# Revit family: RN 56000 Therm-Control-Set di regolazione DN 25 completo
name_source: partatom
category: HLS-Bauteile
units: mm (PartAtom-declared; Revit-internal decimal feet)

## family parameters
Arbeitsebenenbasiert = Nein
Beim Laden mit Abzugskörper schneiden = Nein
Bemaßung runder Anschluss = Durchmesser verwenden
Gemeinsam genutzt = Nein
Immer vertikal = Ja
Klassifizierung = Keine
Raumberechnungspunkt = Nein
Teiletyp = Ventil - Zerlegung in

## types (11) — shared parameters
1.010.00.2 Blattnummer der Richtlinie = 2
1.010.00.3 Ausgabedatum (Monat) der Richtlinie = 201601
1.010.00.4 Herstellername = R. Nussbaum AG
1.010.00.5 Revisionsdatum der Datei = 20190514
1.010.00.6 Webadresse des Herstellers = http://www.nussbaum.ch
1.100.00.3 Sortiernummer für Anzeigereihenfolge = 3
1.100.00.4 Produktbezeichnung = Armaturen für Flächenheizungen
1.960/3L.00.8 Link (URL) = https://www.nussbaum.ch
2.700.00.4 Armaturentyp = 13
2.700.00.5 Nennweite DN = 25
2.700.00.7 Maximale Betriebstemperatur TB [°C] = 60
2.700.00.8 Maximaler Betriebsdruck (Arbeitsdruck) ps [1.0 · 102 Pa] = 6
CONNECTOR0_ref_dY = 27 mm
CONNECTOR1_DIAMETER_dZ_0r = 20 mm
CONNECTOR1_ref_dY = 27 mm
CONNECTOR2_DIAMETER_dX_0r = 25 mm  [stored 0.082021 ft]
CONNECTOR2_dX_00 = 105 mm
CONNECTOR2_dX_01 = 97 mm
CONNECTOR3_DIAMETER_dZ_0r = 20 mm
CONNECTOR4_DIAMETER_dZ_0r = 20 mm
Connector Visibility = Nein
EnclosingSpace Visibility = Nein

## per-type parameters (varying)
- DN 25: 1.800.00.3 TGA-Nummer=0030010000000000000000000000090070000000000000000100000000; 1.810.00.3 Hersteller-Bestellnummer=56000.21; 1.810.00.4 DATANORM-Nummer=56000.21; 1.810.00.6 GTIN-Nummer=7612945814289; 2.700.00.26 Produktbeschreibung=56000.21, Therm-Control-Regelset DN 25 komplett, Grundausstattung, DN=25; CONNECTOR0_DIAMETER_dZ_0r=20 mm; CONNECTOR0_dZ_00=21 mm; CONNECTOR0_dZ_01=28 mm  [stored 0.0918635 ft]; CONNECTOR0_ref_dX=13 mm  [stored 0.0426509 ft]; CONNECTOR0_ref_dZ=28 mm  [stored 0.0918635 ft]; CONNECTOR1_dZ_00=21 mm; CONNECTOR1_dZ_01=28 mm  [stored 0.0918635 ft]; CONNECTOR1_ref_dX=63 mm; CONNECTOR1_ref_dZ=28 mm  [stored 0.0918635 ft]; CONNECTOR2_ref_dX=97 mm; CONNECTOR2_ref_dY=44 mm; CONNECTOR2_ref_dZ=77 mm; CONNECTOR3_dZ_00=119 mm; CONNECTOR3_dZ_01=112 mm; CONNECTOR3_ref_dX=13 mm  [stored 0.0426509 ft]; CONNECTOR3_ref_dY=44 mm; CONNECTOR3_ref_dZ=112 mm; CONNECTOR4_dZ_00=119 mm; CONNECTOR4_dZ_01=112 mm; CONNECTOR4_ref_dX=63 mm; CONNECTOR4_ref_dY=44 mm; CONNECTOR4_ref_dZ=112 mm; CONNECTOR5_DIAMETER_dX_0r=25 mm  [stored 0.082021 ft]; CONNECTOR5_dX_00=105 mm; CONNECTOR5_dX_01=97 mm; CONNECTOR5_ref_dX=97 mm; CONNECTOR5_ref_dY=27 mm; CONNECTOR5_ref_dZ=123 mm; R. Nussbaum AG 56000.21 de Visibility=Ja; R. Nussbaum AG 56000.22 de Visibility=Nein; R. Nussbaum AG 56000.23 de Visibility=Nein; R. Nussbaum AG 56000.24 de Visibility=Nein; R. Nussbaum AG 56000.25 de Visibility=Nein; R. Nussbaum AG 56000.26 de Visibility=Nein; R. Nussbaum AG 56000.27 de Visibility=Nein; R. Nussbaum AG 56000.28 de Visibility=Nein; R. Nussbaum AG 56000.29 de Visibility=Nein; R. Nussbaum AG 56000.30 de Visibility=Nein; R. Nussbaum AG 56000.31 de Visibility=Nein
- DN 25 8: 1.800.00.3 TGA-Nummer=0030010000000000000000000000090070000000000000000200000000; 1.810.00.3 Hersteller-Bestellnummer=56000.22; 1.810.00.4 DATANORM-Nummer=56000.22; 1.810.00.6 GTIN-Nummer=7612945814296; 2.700.00.26 Produktbeschreibung=56000.22, Therm-Control-Regelset DN 25 komplett, Grundausstattung, DN=25; CONNECTOR0_DIAMETER_dZ_0r=20 mm; CONNECTOR0_dZ_00=27 mm; CONNECTOR0_dZ_01=35 mm; CONNECTOR0_ref_dX=10 mm  [stored 0.0328084 ft]; CONNECTOR0_ref_dZ=35 mm; CONNECTOR1_dZ_00=27 mm; CONNECTOR1_dZ_01=35 mm; CONNECTOR1_ref_dX=60 mm; CONNECTOR1_ref_dZ=35 mm; CONNECTOR2_ref_dX=106 mm; CONNECTOR2_ref_dY=27 mm; CONNECTOR2_ref_dZ=35 mm; CONNECTOR3_dZ_00=119 mm; CONNECTOR3_dZ_01=112 mm; CONNECTOR3_ref_dX=100 mm; CONNECTOR3_ref_dY=27 mm; CONNECTOR3_ref_dZ=28 mm  [stored 0.0918635 ft]; CONNECTOR4_dZ_00=113 mm; CONNECTOR4_dZ_01=105 mm; CONNECTOR4_ref_dX=6 mm  [stored 0.019685 ft]; CONNECTOR4_ref_dY=27 mm; CONNECTOR4_ref_dZ=105 mm; CONNECTOR5_DIAMETER_dX_0r=25 mm  [stored 0.082021 ft]; CONNECTOR5_dX_00=105 mm; CONNECTOR5_dX_01=97 mm; CONNECTOR5_ref_dX=56 mm; CONNECTOR5_ref_dY=27 mm; CONNECTOR5_ref_dZ=105 mm; R. Nussbaum AG 56000.21 de Visibility=Nein; R. Nussbaum AG 56000.22 de Visibility=Ja; R. Nussbaum AG 56000.23 de Visibility=Nein; R. Nussbaum AG 56000.24 de Visibility=Nein; R. Nussbaum AG 56000.25 de Visibility=Nein; R. Nussbaum AG 56000.26 de Visibility=Nein; R. Nussbaum AG 56000.27 de Visibility=Nein; R. Nussbaum AG 56000.28 de Visibility=Nein; R. Nussbaum AG 56000.29 de Visibility=Nein; R. Nussbaum AG 56000.30 de Visibility=Nein; R. Nussbaum AG 56000.31 de Visibility=Nein
- DN 25 4: 1.800.00.3 TGA-Nummer=0030010000000000000000000000090070000000000000000300000000; 1.810.00.3 Hersteller-Bestellnummer=56000.23; 1.810.00.4 DATANORM-Nummer=56000.23; 1.810.00.6 GTIN-Nummer=7612945814302; 2.700.00.26 Produktbeschreibung=56000.23, Therm-Control-Regelset DN 25 komplett, Grundausstattung, DN=25; CONNECTOR0_DIAMETER_dZ_0r=15 mm; CONNECTOR0_dZ_00=32 mm  [stored 0.104987 ft]; CONNECTOR0_dZ_01=40 mm; CONNECTOR0_ref_dX=7 mm  [stored 0.0229659 ft]; CONNECTOR0_ref_dZ=40 mm; CONNECTOR1_dZ_00=32 mm  [stored 0.104987 ft]; CONNECTOR1_dZ_01=40 mm; CONNECTOR1_ref_dX=57 mm; CONNECTOR1_ref_dZ=40 mm; CONNECTOR2_ref_dX=107 mm; CONNECTOR2_ref_dY=27 mm; CONNECTOR2_ref_dZ=40 mm; CONNECTOR3_dZ_00=32 mm  [stored 0.104987 ft]; CONNECTOR3_dZ_01=40 mm; CONNECTOR3_ref_dX=157 mm; CONNECTOR3_ref_dY=27 mm; CONNECTOR3_ref_dZ=40 mm; CONNECTOR4_dZ_00=113 mm; CONNECTOR4_dZ_01=105 mm; CONNECTOR4_ref_dX=103 mm; CONNECTOR4_ref_dY=44 mm; CONNECTOR4_ref_dZ=71 mm; CONNECTOR5_DIAMETER_dX_0r=25 mm  [stored 0.082021 ft]; CONNECTOR5_dX_00=105 mm; CONNECTOR5_dX_01=97 mm; CONNECTOR5_ref_dX=104 mm; CONNECTOR5_ref_dY=44 mm; CONNECTOR5_ref_dZ=100 mm; R. Nussbaum AG 56000.21 de Visibility=Nein; R. Nussbaum AG 56000.22 de Visibility=Nein; R. Nussbaum AG 56000.23 de Visibility=Ja; R. Nussbaum AG 56000.24 de Visibility=Nein; R. Nussbaum AG 56000.25 de Visibility=Nein; R. Nussbaum AG 56000.26 de Visibility=Nein; R. Nussbaum AG 56000.27 de Visibility=Nein; R. Nussbaum AG 56000.28 de Visibility=Nein; R. Nussbaum AG 56000.29 de Visibility=Nein; R. Nussbaum AG 56000.30 de Visibility=Nein; R. Nussbaum AG 56000.31 de Visibility=Nein
- DN 25 9: 1.800.00.3 TGA-Nummer=0030010000000000000000000000090070000000000000000400000000; 1.810.00.3 Hersteller-Bestellnummer=56000.24; 1.810.00.4 DATANORM-Nummer=56000.24; 1.810.00.6 GTIN-Nummer=7612945814319; 2.700.00.26 Produktbeschreibung=56000.24, Therm-Control-Regelset DN 25 komplett, Grundausstattung, DN=25; CONNECTOR0_DIAMETER_dZ_0r=20 mm; CONNECTOR0_dZ_00=36 mm; CONNECTOR0_dZ_01=43 mm; CONNECTOR0_ref_dX=5 mm  [stored 0.0164042 ft]; CONNECTOR0_ref_dZ=43 mm; CONNECTOR1_dZ_00=36 mm; CONNECTOR1_dZ_01=43 mm; CONNECTOR1_ref_dX=55 mm; CONNECTOR1_ref_dZ=43 mm; CONNECTOR2_ref_dX=105 mm; CONNECTOR2_ref_dY=27 mm; CONNECTOR2_ref_dZ=43 mm; CONNECTOR3_dZ_00=36 mm; CONNECTOR3_dZ_01=43 mm; CONNECTOR3_ref_dX=155 mm; CONNECTOR3_ref_dY=27 mm; CONNECTOR3_ref_dZ=43 mm; CONNECTOR4_dZ_00=36 mm; CONNECTOR4_dZ_01=43 mm; CONNECTOR4_ref_dX=203 mm; CONNECTOR4_ref_dY=27 mm; CONNECTOR4_ref_dZ=43 mm; CONNECTOR5_DIAMETER_dX_0r=9 mm  [stored 0.0295276 ft]; CONNECTOR5_dX_00=113 mm; CONNECTOR5_dX_01=105 mm; CONNECTOR5_ref_dX=105 mm; CONNECTOR5_ref_dY=27 mm; CONNECTOR5_ref_dZ=35 mm; R. Nussbaum AG 56000.21 de Visibility=Nein; R. Nussbaum AG 56000.22 de Visibility=Nein; R. Nussbaum AG 56000.23 de Visibility=Nein; R. Nussbaum AG 56000.24 de Visibility=Ja; R. Nussbaum AG 56000.25 de Visibility=Nein; R. Nussbaum AG 56000.26 de Visibility=Nein; R. Nussbaum AG 56000.27 de Visibility=Nein; R. Nussbaum AG 56000.28 de Visibility=Nein; R. Nussbaum AG 56000.29 de Visibility=Nein; R. Nussbaum AG 56000.30 de Visibility=Nein; R. Nussbaum AG 56000.31 de Visibility=Nein
- DN 25 2: 1.800.00.3 TGA-Nummer=0030010000000000000000000000090070000000000000000500000000; 1.810.00.3 Hersteller-Bestellnummer=56000.25; 1.810.00.4 DATANORM-Nummer=56000.25; 1.810.00.6 GTIN-Nummer=7612945814326; 2.700.00.26 Produktbeschreibung=56000.25, Therm-Control-Regelset DN 25 komplett, Grundausstattung, DN=25; CONNECTOR0_DIAMETER_dZ_0r=20 mm; CONNECTOR0_dZ_00=39 mm  [stored 0.127953 ft]; CONNECTOR0_dZ_01=46 mm; CONNECTOR0_ref_dX=4 mm  [stored 0.0131234 ft]; CONNECTOR0_ref_dZ=46 mm; CONNECTOR1_dZ_00=39 mm  [stored 0.127953 ft]; CONNECTOR1_dZ_01=46 mm; CONNECTOR1_ref_dX=54 mm; CONNECTOR1_ref_dZ=46 mm; CONNECTOR2_ref_dX=102 mm; CONNECTOR2_ref_dY=27 mm; CONNECTOR2_ref_dZ=46 mm; CONNECTOR3_dZ_00=39 mm  [stored 0.127953 ft]; CONNECTOR3_dZ_01=46 mm; CONNECTOR3_ref_dX=154 mm; CONNECTOR3_ref_dY=27 mm; CONNECTOR3_ref_dZ=46 mm; CONNECTOR4_dZ_00=39 mm  [stored 0.127953 ft]; CONNECTOR4_dZ_01=46 mm; CONNECTOR4_ref_dX=204 mm; CONNECTOR4_ref_dY=27 mm; CONNECTOR4_ref_dZ=46 mm; CONNECTOR5_DIAMETER_dX_0r=9 mm  [stored 0.0295276 ft]; CONNECTOR5_dX_00=113 mm; CONNECTOR5_dX_01=105 mm; CONNECTOR5_ref_dX=254 mm; CONNECTOR5_ref_dY=27 mm; CONNECTOR5_ref_dZ=46 mm; R. Nussbaum AG 56000.21 de Visibility=Nein; R. Nussbaum AG 56000.22 de Visibility=Nein; R. Nussbaum AG 56000.23 de Visibility=Nein; R. Nussbaum AG 56000.24 de Visibility=Nein; R. Nussbaum AG 56000.25 de Visibility=Ja; R. Nussbaum AG 56000.26 de Visibility=Nein; R. Nussbaum AG 56000.27 de Visibility=Nein; R. Nussbaum AG 56000.28 de Visibility=Nein; R. Nussbaum AG 56000.29 de Visibility=Nein; R. Nussbaum AG 56000.30 de Visibility=Nein; R. Nussbaum AG 56000.31 de Visibility=Nein
- DN 25 1: 1.800.00.3 TGA-Nummer=0030010000000000000000000000090070000000000000000600000000; 1.810.00.3 Hersteller-Bestellnummer=56000.26; 1.810.00.4 DATANORM-Nummer=56000.26; 1.810.00.6 GTIN-Nummer=7612945814333; 2.700.00.26 Produktbeschreibung=56000.26, Therm-Control-Regelset DN 25 komplett, Grundausstattung, DN=25; CONNECTOR0_DIAMETER_dZ_0r=20 mm; CONNECTOR0_dZ_00=41 mm; CONNECTOR0_dZ_01=49 mm; CONNECTOR0_ref_dX=2 mm  [stored 0.00656168 ft]; CONNECTOR0_ref_dZ=49 mm; CONNECTOR1_dZ_00=41 mm; CONNECTOR1_dZ_01=49 mm; CONNECTOR1_ref_dX=52 mm; CONNECTOR1_ref_dZ=49 mm; CONNECTOR2_ref_dX=101 mm; CONNECTOR2_ref_dY=27 mm; CONNECTOR2_ref_dZ=49 mm; CONNECTOR3_dZ_00=41 mm; CONNECTOR3_dZ_01=49 mm; CONNECTOR3_ref_dX=152 mm; CONNECTOR3_ref_dY=27 mm; CONNECTOR3_ref_dZ=49 mm; CONNECTOR4_dZ_00=41 mm; CONNECTOR4_dZ_01=49 mm; CONNECTOR4_ref_dX=202 mm; CONNECTOR4_ref_dY=27 mm; CONNECTOR4_ref_dZ=49 mm; CONNECTOR5_DIAMETER_dX_0r=9 mm  [stored 0.0295276 ft]; CONNECTOR5_dX_00=113 mm; CONNECTOR5_dX_01=105 mm; CONNECTOR5_ref_dX=251 mm; CONNECTOR5_ref_dY=27 mm; CONNECTOR5_ref_dZ=49 mm; R. Nussbaum AG 56000.21 de Visibility=Nein; R. Nussbaum AG 56000.22 de Visibility=Nein; R. Nussbaum AG 56000.23 de Visibility=Nein; R. Nussbaum AG 56000.24 de Visibility=Nein; R. Nussbaum AG 56000.25 de Visibility=Nein; R. Nussbaum AG 56000.26 de Visibility=Ja; R. Nussbaum AG 56000.27 de Visibility=Nein; R. Nussbaum AG 56000.28 de Visibility=Nein; R. Nussbaum AG 56000.29 de Visibility=Nein; R. Nussbaum AG 56000.30 de Visibility=Nein; R. Nussbaum AG 56000.31 de Visibility=Nein
- DN 25 5: 1.800.00.3 TGA-Nummer=0030010000000000000000000000090070000000000000000700000000; 1.810.00.3 Hersteller-Bestellnummer=56000.27; 1.810.00.4 DATANORM-Nummer=56000.27; 1.810.00.6 GTIN-Nummer=7612945814340; 2.700.00.26 Produktbeschreibung=56000.27, Therm-Control-Regelset DN 25 komplett, Grundausstattung, DN=25; CONNECTOR0_DIAMETER_dZ_0r=20 mm; CONNECTOR0_dZ_00=43 mm; CONNECTOR0_dZ_01=51 mm; CONNECTOR0_ref_dX=1 mm  [stored 0.00328084 ft]; CONNECTOR0_ref_dZ=51 mm; CONNECTOR1_dZ_00=43 mm; CONNECTOR1_dZ_01=51 mm; CONNECTOR1_ref_dX=51 mm; CONNECTOR1_ref_dZ=51 mm; CONNECTOR2_ref_dX=100 mm; CONNECTOR2_ref_dY=27 mm; CONNECTOR2_ref_dZ=51 mm; CONNECTOR3_dZ_00=43 mm; CONNECTOR3_dZ_01=51 mm; CONNECTOR3_ref_dX=151 mm; CONNECTOR3_ref_dY=27 mm; CONNECTOR3_ref_dZ=51 mm; CONNECTOR4_dZ_00=43 mm; CONNECTOR4_dZ_01=51 mm; CONNECTOR4_ref_dX=201 mm; CONNECTOR4_ref_dY=27 mm; CONNECTOR4_ref_dZ=51 mm; CONNECTOR5_DIAMETER_dX_0r=9 mm  [stored 0.0295276 ft]; CONNECTOR5_dX_00=113 mm; CONNECTOR5_dX_01=105 mm; CONNECTOR5_ref_dX=250 mm; CONNECTOR5_ref_dY=27 mm; CONNECTOR5_ref_dZ=51 mm; R. Nussbaum AG 56000.21 de Visibility=Nein; R. Nussbaum AG 56000.22 de Visibility=Nein; R. Nussbaum AG 56000.23 de Visibility=Nein; R. Nussbaum AG 56000.24 de Visibility=Nein; R. Nussbaum AG 56000.25 de Visibility=Nein; R. Nussbaum AG 56000.26 de Visibility=Nein; R. Nussbaum AG 56000.27 de Visibility=Ja; R. Nussbaum AG 56000.28 de Visibility=Nein; R. Nussbaum AG 56000.29 de Visibility=Nein; R. Nussbaum AG 56000.30 de Visibility=Nein; R. Nussbaum AG 56000.31 de Visibility=Nein
- DN 25 10: 1.800.00.3 TGA-Nummer=0030010000000000000000000000090070000000000000000800000000; 1.810.00.3 Hersteller-Bestellnummer=56000.28; 1.810.00.4 DATANORM-Nummer=56000.28; 1.810.00.6 GTIN-Nummer=7612945814357; 2.700.00.26 Produktbeschreibung=56000.28, Therm-Control-Regelset DN 25 komplett, Grundausstattung, DN=25; CONNECTOR0_DIAMETER_dZ_0r=20 mm; CONNECTOR0_dZ_00=45 mm; CONNECTOR0_dZ_01=53 mm; CONNECTOR0_ref_dX=1 mm  [stored 0.00328084 ft]; CONNECTOR0_ref_dZ=53 mm; CONNECTOR1_dZ_00=45 mm; CONNECTOR1_dZ_01=53 mm; CONNECTOR1_ref_dX=50 mm; CONNECTOR1_ref_dZ=53 mm; CONNECTOR2_ref_dX=100 mm; CONNECTOR2_ref_dY=27 mm; CONNECTOR2_ref_dZ=53 mm; CONNECTOR3_dZ_00=45 mm; CONNECTOR3_dZ_01=53 mm; CONNECTOR3_ref_dX=150 mm; CONNECTOR3_ref_dY=27 mm; CONNECTOR3_ref_dZ=53 mm; CONNECTOR4_dZ_00=45 mm; CONNECTOR4_dZ_01=53 mm; CONNECTOR4_ref_dX=200 mm; CONNECTOR4_ref_dY=27 mm; CONNECTOR4_ref_dZ=53 mm; CONNECTOR5_DIAMETER_dX_0r=9 mm  [stored 0.0295276 ft]; CONNECTOR5_dX_00=113 mm; CONNECTOR5_dX_01=105 mm; CONNECTOR5_ref_dX=250 mm; CONNECTOR5_ref_dY=27 mm; CONNECTOR5_ref_dZ=53 mm; R. Nussbaum AG 56000.21 de Visibility=Nein; R. Nussbaum AG 56000.22 de Visibility=Nein; R. Nussbaum AG 56000.23 de Visibility=Nein; R. Nussbaum AG 56000.24 de Visibility=Nein; R. Nussbaum AG 56000.25 de Visibility=Nein; R. Nussbaum AG 56000.26 de Visibility=Nein; R. Nussbaum AG 56000.27 de Visibility=Nein; R. Nussbaum AG 56000.28 de Visibility=Ja; R. Nussbaum AG 56000.29 de Visibility=Nein; R. Nussbaum AG 56000.30 de Visibility=Nein; R. Nussbaum AG 56000.31 de Visibility=Nein
- DN 25 6: 1.800.00.3 TGA-Nummer=0030010000000000000000000000090070000000000000000900000000; 1.810.00.3 Hersteller-Bestellnummer=56000.29; 1.810.00.4 DATANORM-Nummer=56000.29; 1.810.00.6 GTIN-Nummer=7612945814364; 2.700.00.26 Produktbeschreibung=56000.29, Therm-Control-Regelset DN 25 komplett, Grundausstattung, DN=25; CONNECTOR0_DIAMETER_dZ_0r=20 mm; CONNECTOR0_dZ_00=47 mm; CONNECTOR0_dZ_01=54 mm; CONNECTOR0_ref_dX=1 mm  [stored 0.00328084 ft]; CONNECTOR0_ref_dZ=54 mm; CONNECTOR1_dZ_00=47 mm; CONNECTOR1_dZ_01=54 mm; CONNECTOR1_ref_dX=50 mm; CONNECTOR1_ref_dZ=54 mm; CONNECTOR2_ref_dX=99 mm; CONNECTOR2_ref_dY=27 mm; CONNECTOR2_ref_dZ=54 mm; CONNECTOR3_dZ_00=47 mm; CONNECTOR3_dZ_01=54 mm; CONNECTOR3_ref_dX=150 mm; CONNECTOR3_ref_dY=27 mm; CONNECTOR3_ref_dZ=54 mm; CONNECTOR4_dZ_00=47 mm; CONNECTOR4_dZ_01=54 mm; CONNECTOR4_ref_dX=200 mm; CONNECTOR4_ref_dY=27 mm; CONNECTOR4_ref_dZ=54 mm; CONNECTOR5_DIAMETER_dX_0r=9 mm  [stored 0.0295276 ft]; CONNECTOR5_dX_00=113 mm; CONNECTOR5_dX_01=105 mm; CONNECTOR5_ref_dX=249 mm; CONNECTOR5_ref_dY=27 mm; CONNECTOR5_ref_dZ=54 mm; R. Nussbaum AG 56000.21 de Visibility=Nein; R. Nussbaum AG 56000.22 de Visibility=Nein; R. Nussbaum AG 56000.23 de Visibility=Nein; R. Nussbaum AG 56000.24 de Visibility=Nein; R. Nussbaum AG 56000.25 de Visibility=Nein; R. Nussbaum AG 56000.26 de Visibility=Nein; R. Nussbaum AG 56000.27 de Visibility=Nein; R. Nussbaum AG 56000.28 de Visibility=Nein; R. Nussbaum AG 56000.29 de Visibility=Ja; R. Nussbaum AG 56000.30 de Visibility=Nein; R. Nussbaum AG 56000.31 de Visibility=Nein
- DN 25 3: 1.800.00.3 TGA-Nummer=0030010000000000000000000000090070000000000000001000000000; 1.810.00.3 Hersteller-Bestellnummer=56000.30; 1.810.00.4 DATANORM-Nummer=56000.30; 1.810.00.6 GTIN-Nummer=7612945814371; 2.700.00.26 Produktbeschreibung=56000.30, Therm-Control-Regelset DN 25 komplett, Grundausstattung, DN=25; CONNECTOR0_DIAMETER_dZ_0r=19 mm; CONNECTOR0_dZ_00=48 mm; CONNECTOR0_dZ_01=56 mm; CONNECTOR0_ref_dX=1 mm  [stored 0.00328084 ft]; CONNECTOR0_ref_dZ=56 mm; CONNECTOR1_dZ_00=48 mm; CONNECTOR1_dZ_01=56 mm; CONNECTOR1_ref_dX=49 mm; CONNECTOR1_ref_dZ=56 mm; CONNECTOR2_ref_dX=98 mm; CONNECTOR2_ref_dY=27 mm; CONNECTOR2_ref_dZ=56 mm; CONNECTOR3_dZ_00=48 mm; CONNECTOR3_dZ_01=56 mm; CONNECTOR3_ref_dX=149 mm; CONNECTOR3_ref_dY=27 mm; CONNECTOR3_ref_dZ=56 mm; CONNECTOR4_dZ_00=48 mm; CONNECTOR4_dZ_01=56 mm; CONNECTOR4_ref_dX=199 mm; CONNECTOR4_ref_dY=27 mm; CONNECTOR4_ref_dZ=56 mm; CONNECTOR5_DIAMETER_dX_0r=9 mm  [stored 0.0295276 ft]; CONNECTOR5_dX_00=113 mm; CONNECTOR5_dX_01=105 mm; CONNECTOR5_ref_dX=248 mm; CONNECTOR5_ref_dY=27 mm; CONNECTOR5_ref_dZ=56 mm; R. Nussbaum AG 56000.21 de Visibility=Nein; R. Nussbaum AG 56000.22 de Visibility=Nein; R. Nussbaum AG 56000.23 de Visibility=Nein; R. Nussbaum AG 56000.24 de Visibility=Nein; R. Nussbaum AG 56000.25 de Visibility=Nein; R. Nussbaum AG 56000.26 de Visibility=Nein; R. Nussbaum AG 56000.27 de Visibility=Nein; R. Nussbaum AG 56000.28 de Visibility=Nein; R. Nussbaum AG 56000.29 de Visibility=Nein; R. Nussbaum AG 56000.30 de Visibility=Ja; R. Nussbaum AG 56000.31 de Visibility=Nein
- DN 25 7: 1.800.00.3 TGA-Nummer=0030010000000000000000000000090070000000000000001100000000; 1.810.00.3 Hersteller-Bestellnummer=56000.31; 1.810.00.4 DATANORM-Nummer=56000.31; 1.810.00.6 GTIN-Nummer=7612945814388; 2.700.00.26 Produktbeschreibung=56000.31, Therm-Control-Regelset DN 25 komplett, Grundausstattung, DN=25; CONNECTOR0_DIAMETER_dZ_0r=21 mm; CONNECTOR0_dZ_00=49 mm; CONNECTOR0_dZ_01=57 mm; CONNECTOR0_ref_dX=2 mm  [stored 0.00656168 ft]; CONNECTOR0_ref_dZ=57 mm; CONNECTOR1_dZ_00=49 mm; CONNECTOR1_dZ_01=57 mm; CONNECTOR1_ref_dX=48 mm; CONNECTOR1_ref_dZ=57 mm; CONNECTOR2_ref_dX=98 mm; CONNECTOR2_ref_dY=27 mm; CONNECTOR2_ref_dZ=57 mm; CONNECTOR3_dZ_00=49 mm; CONNECTOR3_dZ_01=57 mm; CONNECTOR3_ref_dX=148 mm; CONNECTOR3_ref_dY=27 mm; CONNECTOR3_ref_dZ=57 mm; CONNECTOR4_dZ_00=49 mm; CONNECTOR4_dZ_01=57 mm; CONNECTOR4_ref_dX=198 mm; CONNECTOR4_ref_dY=27 mm; CONNECTOR4_ref_dZ=57 mm; CONNECTOR5_DIAMETER_dX_0r=9 mm  [stored 0.0295276 ft]; CONNECTOR5_dX_00=113 mm; CONNECTOR5_dX_01=105 mm; CONNECTOR5_ref_dX=248 mm; CONNECTOR5_ref_dY=27 mm; CONNECTOR5_ref_dZ=57 mm; R. Nussbaum AG 56000.21 de Visibility=Nein; R. Nussbaum AG 56000.22 de Visibility=Nein; R. Nussbaum AG 56000.23 de Visibility=Nein; R. Nussbaum AG 56000.24 de Visibility=Nein; R. Nussbaum AG 56000.25 de Visibility=Nein; R. Nussbaum AG 56000.26 de Visibility=Nein; R. Nussbaum AG 56000.27 de Visibility=Nein; R. Nussbaum AG 56000.28 de Visibility=Nein; R. Nussbaum AG 56000.29 de Visibility=Nein; R. Nussbaum AG 56000.30 de Visibility=Nein; R. Nussbaum AG 56000.31 de Visibility=Ja

note: [stored X ft] marks values corroborated as IEEE doubles in the binary element streams (Revit-internal decimal feet)

## geometry (parser evidence)
native form markers: Sweep x2
no freeform markers — native parametric forms only
